# Revit family: Тумба выкатная 3 ящика Юнитекс ПФ ПТ
name_source: partatom
category: Оборудование
revit_build: Autodesk Revit 2017 (Build: 20170118_1100(x64)
units: mm (PartAtom-declared; Revit-internal decimal feet)

## family parameters
Всегда вертикально = Да
Заголовок OmniClass = General Furniture and Specialties
На основе рабочей плоскости = Нет
Номер OmniClass = 23.40.20.00
Общий = Нет
При загрузке вырезать с полостями = Нет
Размер круглого соединителя = Использовать диаметр
Тип детали = Нормальный
Точка расчета площади = Нет

## types (3) — shared parameters
Изготовитель = ОАО «1470 УМТО» - производственная база «27ДОЗ» 121471 г. Москва, ул.Гжатская д.9. Тел:(495)443-62-26 Сайт: пэу.рф
Общ_Единицы измерения = шт.
Общ_Поставщик = Юнитекс
Общ_Ширина = 420 мм

## per-type parameters (varying)
| type | Общ_Высота | Общ_Глубина | Общ_Наименование | Общ_Тип, марка |
| Тумба выкатная 3-ящичная с центральным замком ПФ | 590 мм | 530 мм | Тумба выкатная 3-ящичная с центральным замком | ПК 918 |
| Тумба выкатная 3-ящичная с замком ПФ | 590 мм | 530 мм | Тумба выкатная 3-ящичная с замком | ПК 781 |
| Тумба к столу руководителя ПТ | 600 мм | 520 мм | Тумба выкатная с прямоугольной крышкой 3-ящичная с центральным замком | ПТ 213 |
